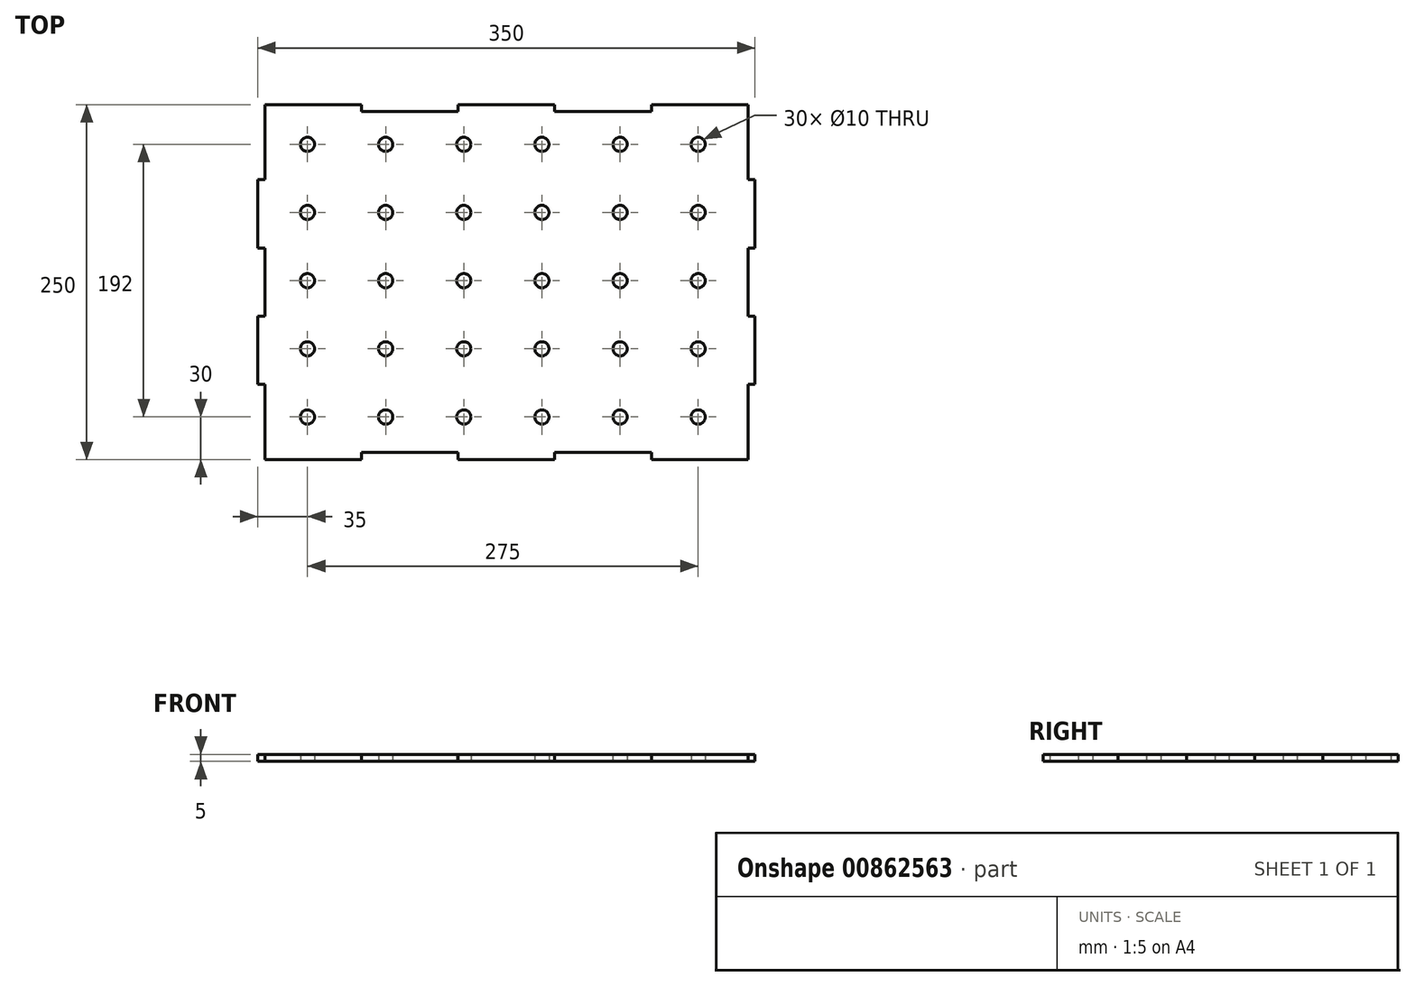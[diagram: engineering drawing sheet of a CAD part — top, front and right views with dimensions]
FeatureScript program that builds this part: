
annotation { "Feature Type Name" : "Feature", "Feature Type Description" : "" }
export const myFeature = defineFeature(function(context is Context, id is Id, definition is map)
    precondition{}
    {
        {
            var Q0;
            Q0=qCreatedBy(makeId("Top.planeOp"),FACE);
            var sketch = newSketch(context, id + "F0", { "sketchPlane" : qUnion([Q0])});
            skLineSegment(sketch, "E0.bottom", {"start": v(170, -120) * mm, "end": v(-170, -120) * mm});
            skLineSegment(sketch, "E0.top", {"start": v(170, 120) * mm, "end": v(-170, 120) * mm});
            skLineSegment(sketch, "E0.left", {"start": v(170, -120) * mm, "end": v(170, 120) * mm});
            skLineSegment(sketch, "E0.right", {"start": v(-170, -120) * mm, "end": v(-170, 120) * mm});
            skPoint(sketch, "E0.middle", {"position": v(0, 0) * mm});
            skLineSegment(sketch, "E1", {"start": v(-170, -120) * mm, "end": v(-170, -125) * mm});
            skLineSegment(sketch, "E2", {"start": v(-170, -125) * mm, "end": v(-102, -125) * mm});
            skLineSegment(sketch, "E3", {"start": v(-102, -125) * mm, "end": v(-102, -120) * mm});
            skLineSegment(sketch, "E4.1.0.0", {"start": v(34, -125) * mm, "end": v(34, -120) * mm});
            skLineSegment(sketch, "E4.1.0.1", {"start": v(-34, -120) * mm, "end": v(-34, -125) * mm});
            skLineSegment(sketch, "E4.1.0.2", {"start": v(-34, -125) * mm, "end": v(34, -125) * mm});
            skLineSegment(sketch, "E4.2.0.0", {"start": v(170, -125) * mm, "end": v(170, -120) * mm});
            skLineSegment(sketch, "E4.2.0.1", {"start": v(102, -120) * mm, "end": v(102, -125) * mm});
            skLineSegment(sketch, "E4.2.0.2", {"start": v(102, -125) * mm, "end": v(170, -125) * mm});
            skLineSegment(sketch, "E4.direction1", {"start": v(-170, -125) * mm, "end": v(-34, -125) * mm, "construction": true});
            skLineSegment(sketch, "E5.MirrorCS", {"start": v(-170, 120) * mm, "end": v(-170, 125) * mm});
            skLineSegment(sketch, "E6.MirrorCS", {"start": v(-34, 120) * mm, "end": v(-34, 125) * mm});
            skLineSegment(sketch, "E7.MirrorCS", {"start": v(170, 125) * mm, "end": v(170, 120) * mm});
            skLineSegment(sketch, "E8.MirrorCS", {"start": v(-102, 125) * mm, "end": v(-102, 120) * mm});
            skLineSegment(sketch, "E9.MirrorCS", {"start": v(102, 120) * mm, "end": v(102, 125) * mm});
            skLineSegment(sketch, "E10.MirrorCS", {"start": v(34, 125) * mm, "end": v(34, 120) * mm});
            skLineSegment(sketch, "E11.MirrorCS", {"start": v(-170, 125) * mm, "end": v(-102, 125) * mm});
            skLineSegment(sketch, "E12.MirrorCS", {"start": v(-170, 125) * mm, "end": v(-34, 125) * mm, "construction": true});
            skLineSegment(sketch, "E13.MirrorCS", {"start": v(-34, 125) * mm, "end": v(34, 125) * mm});
            skLineSegment(sketch, "E14.MirrorCS", {"start": v(102, 125) * mm, "end": v(170, 125) * mm});
            skLineSegment(sketch, "E15", {"start": v(-170, 72) * mm, "end": v(-175, 72) * mm});
            skLineSegment(sketch, "E16", {"start": v(-175, 72) * mm, "end": v(-175, 24) * mm});
            skLineSegment(sketch, "E17", {"start": v(-175, 24) * mm, "end": v(-170, 24) * mm});
            skLineSegment(sketch, "E18.0.1.0", {"start": v(-170, -24) * mm, "end": v(-175, -24) * mm});
            skLineSegment(sketch, "E18.0.1.1", {"start": v(-175, -24) * mm, "end": v(-175, -72) * mm});
            skLineSegment(sketch, "E18.0.1.2", {"start": v(-175, -72) * mm, "end": v(-170, -72) * mm});
            skLineSegment(sketch, "E18.direction2", {"start": v(-175, 72) * mm, "end": v(-175, -24) * mm, "construction": true});
            skLineSegment(sketch, "E19.MirrorCS", {"start": v(170, 72) * mm, "end": v(175, 72) * mm});
            skLineSegment(sketch, "E20.MirrorCS", {"start": v(170, -24) * mm, "end": v(175, -24) * mm});
            skLineSegment(sketch, "E21.MirrorCS", {"start": v(175, -72) * mm, "end": v(170, -72) * mm});
            skLineSegment(sketch, "E22.MirrorCS", {"start": v(175, 24) * mm, "end": v(170, 24) * mm});
            skLineSegment(sketch, "E23.MirrorCS", {"start": v(175, 72) * mm, "end": v(175, 24) * mm});
            skLineSegment(sketch, "E24.MirrorCS", {"start": v(175, 72) * mm, "end": v(175, -24) * mm, "construction": true});
            skLineSegment(sketch, "E25.MirrorCS", {"start": v(175, -24) * mm, "end": v(175, -72) * mm});
            skCircle(sketch, "E26", {"center": v(-140, -95) * mm, "radius": 5 * mm});
            skCircle(sketch, "E27.0.1.0", {"center": v(-140, -47) * mm, "radius": 5 * mm});
            skCircle(sketch, "E27.0.2.0", {"center": v(-140, 1) * mm, "radius": 5 * mm});
            skCircle(sketch, "E27.0.3.0", {"center": v(-140, 49) * mm, "radius": 5 * mm});
            skCircle(sketch, "E27.0.4.0", {"center": v(-140, 97) * mm, "radius": 5 * mm});
            skCircle(sketch, "E27.1.0.0", {"center": v(-85, -95) * mm, "radius": 5 * mm});
            skCircle(sketch, "E27.1.1.0", {"center": v(-85, -47) * mm, "radius": 5 * mm});
            skCircle(sketch, "E27.1.2.0", {"center": v(-85, 1) * mm, "radius": 5 * mm});
            skCircle(sketch, "E27.1.3.0", {"center": v(-85, 49) * mm, "radius": 5 * mm});
            skCircle(sketch, "E27.1.4.0", {"center": v(-85, 97) * mm, "radius": 5 * mm});
            skCircle(sketch, "E27.2.0.0", {"center": v(-30, -95) * mm, "radius": 5 * mm});
            skCircle(sketch, "E27.2.1.0", {"center": v(-30, -47) * mm, "radius": 5 * mm});
            skCircle(sketch, "E27.2.2.0", {"center": v(-30, 1) * mm, "radius": 5 * mm});
            skCircle(sketch, "E27.2.3.0", {"center": v(-30, 49) * mm, "radius": 5 * mm});
            skCircle(sketch, "E27.2.4.0", {"center": v(-30, 97) * mm, "radius": 5 * mm});
            skCircle(sketch, "E27.3.0.0", {"center": v(25, -95) * mm, "radius": 5 * mm});
            skCircle(sketch, "E27.3.1.0", {"center": v(25, -47) * mm, "radius": 5 * mm});
            skCircle(sketch, "E27.3.2.0", {"center": v(25, 1) * mm, "radius": 5 * mm});
            skCircle(sketch, "E27.3.3.0", {"center": v(25, 49) * mm, "radius": 5 * mm});
            skCircle(sketch, "E27.3.4.0", {"center": v(25, 97) * mm, "radius": 5 * mm});
            skCircle(sketch, "E27.4.0.0", {"center": v(80, -95) * mm, "radius": 5 * mm});
            skCircle(sketch, "E27.4.1.0", {"center": v(80, -47) * mm, "radius": 5 * mm});
            skCircle(sketch, "E27.4.2.0", {"center": v(80, 1) * mm, "radius": 5 * mm});
            skCircle(sketch, "E27.4.3.0", {"center": v(80, 49) * mm, "radius": 5 * mm});
            skCircle(sketch, "E27.4.4.0", {"center": v(80, 97) * mm, "radius": 5 * mm});
            skCircle(sketch, "E27.5.0.0", {"center": v(135, -95) * mm, "radius": 5 * mm});
            skCircle(sketch, "E27.5.1.0", {"center": v(135, -47) * mm, "radius": 5 * mm});
            skCircle(sketch, "E27.5.2.0", {"center": v(135, 1) * mm, "radius": 5 * mm});
            skCircle(sketch, "E27.5.3.0", {"center": v(135, 49) * mm, "radius": 5 * mm});
            skCircle(sketch, "E27.5.4.0", {"center": v(135, 97) * mm, "radius": 5 * mm});
            skLineSegment(sketch, "E27.direction1", {"start": v(-140, -95) * mm, "end": v(-85, -95) * mm, "construction": true});
            skLineSegment(sketch, "E27.direction2", {"start": v(-140, -95) * mm, "end": v(-140, -47) * mm, "construction": true});
            skSolve(sketch);
        }
        {
            var Q0;
            Q0 = qSketchRegion(id + "F0", true);
            extrude(context, id + "F1", {"entities" : qUnion([Q0]), "depth" : 5 * mm, "offsetDistance" : 25 * mm});
        }
    });
